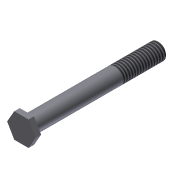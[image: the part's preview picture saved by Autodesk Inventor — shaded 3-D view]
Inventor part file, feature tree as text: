
AUTODESK INVENTOR PART (.ipt)
format: ipt  version: 2011 (Build 150239000, 239)  size: 89,600 bytes
history: native  units: in
note: dims shown in document units (in); Inventor stores cm internally (conversion verified against a paired STEP export)
features: extrude x2, sketch x2, thread x1, chamfer x1
ambient origin geometry x8: Origin, YZ Plane, XZ Plane, XY Plane, X Axis, Y Axis, Z Axis, Center Point
bodies: Solid1 (feature_tree)
feature tree (6):
  extrude  "Extrusion1"  Depth=3.0in TaperAngle=0.0deg
  extrude  "Extrusion2"  Depth=0.125in TaperAngle=0.0deg
  thread  "Thread1"  [1 undecoded]
  chamfer  "Chamfer1"  Distance=0.02in Angle=45.0deg
  sketch  "Sketch1"  dims[d0=0.375in d1=3.0in d2=0.0in]
  sketch  "Sketch2"  dims[d3=0.5625in d4=0.125in d5=0.0in d6=1.0in d7=0.0in d8=0.02in d9=0.125in d10=45.0deg]
note: 1 required parameter value undecoded (feature->parameter linkage not recoverable at this tier; creation-order binding heuristic only, values carry confidence <= 0.55)
